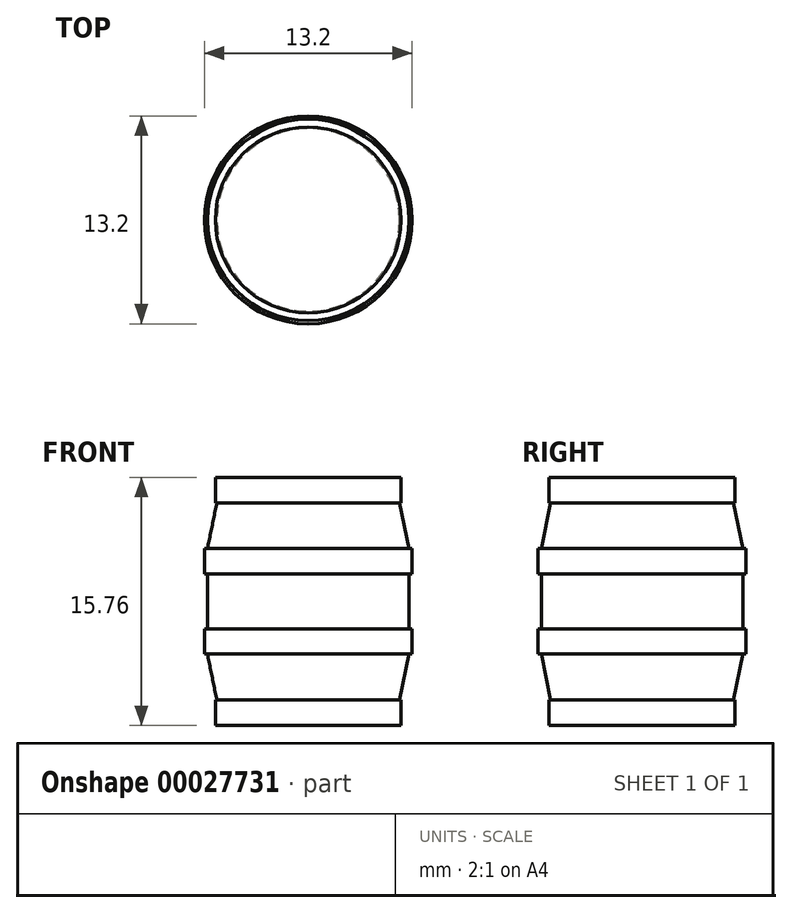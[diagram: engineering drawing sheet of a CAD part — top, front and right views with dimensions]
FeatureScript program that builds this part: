
annotation { "Feature Type Name" : "Feature", "Feature Type Description" : "" }
export const myFeature = defineFeature(function(context is Context, id is Id, definition is map)
    precondition{}
    {
        {
            var Q0;
            Q0=qCreatedBy(makeId("Top.planeOp"),FACE);
            var sketch = newSketch(context, id + "F0", { "sketchPlane" : qUnion([Q0])});
            skCircle(sketch, "E0", {"center": v(0, 0) * mm, "radius": 5.9 * mm});
            skSolve(sketch);
        }
        {
            var Q0;
            Q0 = qSketchRegion(id + "F0", true);
            extrude(context, id + "F1", {"entities" : qUnion([Q0]), "depth" : 1.63 * mm});
        }
        {
            var Q0;
            Q0=qCreatedBy(makeId("Front.planeOp"),FACE);
            var sketch = newSketch(context, id + "F2", { "sketchPlane" : qUnion([Q0])});
            skLineSegment(sketch, "E1", {"start": v(0, 1.63) * mm, "end": v(0, 4.53) * mm});
            skLineSegment(sketch, "E2", {"start": v(0, 4.53) * mm, "end": v(6.4, 4.53) * mm});
            skLineSegment(sketch, "E3", {"start": v(0, 1.63) * mm, "end": v(5.8, 1.63) * mm});
            skLineSegment(sketch, "E4", {"start": v(5.8, 1.63) * mm, "end": v(6.4, 4.53) * mm});
            skSolve(sketch);
        }
        {
            var Q0;
            Q0 = qSketchRegion(id + "F2", true);
            var Q1;
            Q1=sQuery(id+"F2.wireOp",EDGE,"E1");
            revolve(context, id + "F3", {"operationType" : NewBodyOperationType.ADD, "entities" : qUnion([Q0]), "axis" : qUnion([Q1]), "revolveType" : RevolveType.FULL});
        }
        {
            var Q0;
            Q0=makeQuery(id+"F3.opRevolve","SWEPT_FACE",FACE,{"disambiguationData":[OSD([sQuery(id+"F2.wireOp",EDGE,"E2")])]});
            var sketch = newSketch(context, id + "F4", { "sketchPlane" : qUnion([Q0])});
            skCircle(sketch, "E5", {"center": v(0, 0) * mm, "radius": 6.6 * mm});
            skSolve(sketch);
        }
        {
            var Q0;
            Q0 = qSketchRegion(id + "F4", true);
            extrude(context, id + "F5", {"entities" : qUnion([Q0]), "operationType" : NewBodyOperationType.ADD, "depth" : 1.6 * mm});
        }
        {
            var Q0;
            Q0=makeQuery(id+"F5.opExtrude","CAP_FACE",FACE,{"disambiguationData":[OSD([sQuery(id+"F4.wireOp",EDGE,"E5")])],"isStart":false});
            var sketch = newSketch(context, id + "F6", { "sketchPlane" : qUnion([Q0])});
            skCircle(sketch, "E6", {"center": v(0, 0) * mm, "radius": 6.4 * mm});
            skSolve(sketch);
        }
        {
            var Q0;
            Q0 = qSketchRegion(id + "F6", true);
            extrude(context, id + "F7", {"entities" : qUnion([Q0]), "operationType" : NewBodyOperationType.ADD, "depth" : 1.75 * mm});
        }
        {
            var Q0;
            Q0=makeQuery(id+"F1.opExtrude","SWEPT_BODY",BODY,{"disambiguationData":[OSD([sQuery(id+"F0.wireOp",EDGE,"E0")])]});
            var Q1;
            Q1=makeQuery(id+"F7.opExtrude","CAP_FACE",FACE,{"disambiguationData":[OSD([sQuery(id+"F6.wireOp",EDGE,"E6")])],"isStart":false});
            mirror(context, id + "F8", {"operationType" : NewBodyOperationType.ADD, "entities" : qUnion([Q0]), "mirrorPlane" : qUnion([Q1])});
        }
    });
